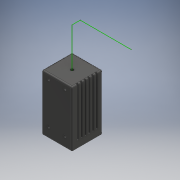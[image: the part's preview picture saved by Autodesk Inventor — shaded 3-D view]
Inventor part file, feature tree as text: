
AUTODESK INVENTOR PART (.ipt)
format: ipt  version: 2017 (Build 210142000, 142)  size: 310,784 bytes
history: native  units: mm
features: sketch x10, extrude x7, hole x2, pattern_circular x1, mirror x1, fillet x1
ambient origin geometry x8: Origin, YZ Plane, XZ Plane, XY Plane, X Axis, Y Axis, Z Axis, Center Point
bodies: Solide1 (feature_tree)
feature tree (22):
  extrude  "Extrusion1"  Depth=30.0mm
  hole  "Perçage1"  [1 undecoded]
  extrude  "Extrusion2"  Depth=55.0mm TaperAngle=0.0deg
  extrude  "Extrusion3"  Depth=40.0mm
  extrude  "Extrusion4"  Depth=16.0mm
  pattern_circular  "Réseau circulaire1"  [2 undecoded]
  mirror  "Symétrie1"
  fillet  "Congé1"  Radius=5.0mm
  extrude  "Extrusion8"  Depth=3.0mm
  extrude  "Extrusion5"  Depth=10.0mm TaperAngle=0.0deg
  extrude  "Extrusion6"  Depth=1.5mm
  sketch  "Esquisse11"
  hole  "Perçage2"  [1 undecoded]
  sketch  "Esquisse1"
  sketch  "Esquisse2"
  sketch  "Esquisse3"
  sketch  "Esquisse4"
  sketch  "Esquisse5"
  sketch  "Esquisse6"
  sketch  "Esquisse7"
  sketch  "Esquisse9"
  sketch  "Esquisse12"
note: 4 required parameter values undecoded (feature->parameter linkage not recoverable at this tier; creation-order binding heuristic only, values carry confidence <= 0.55)
